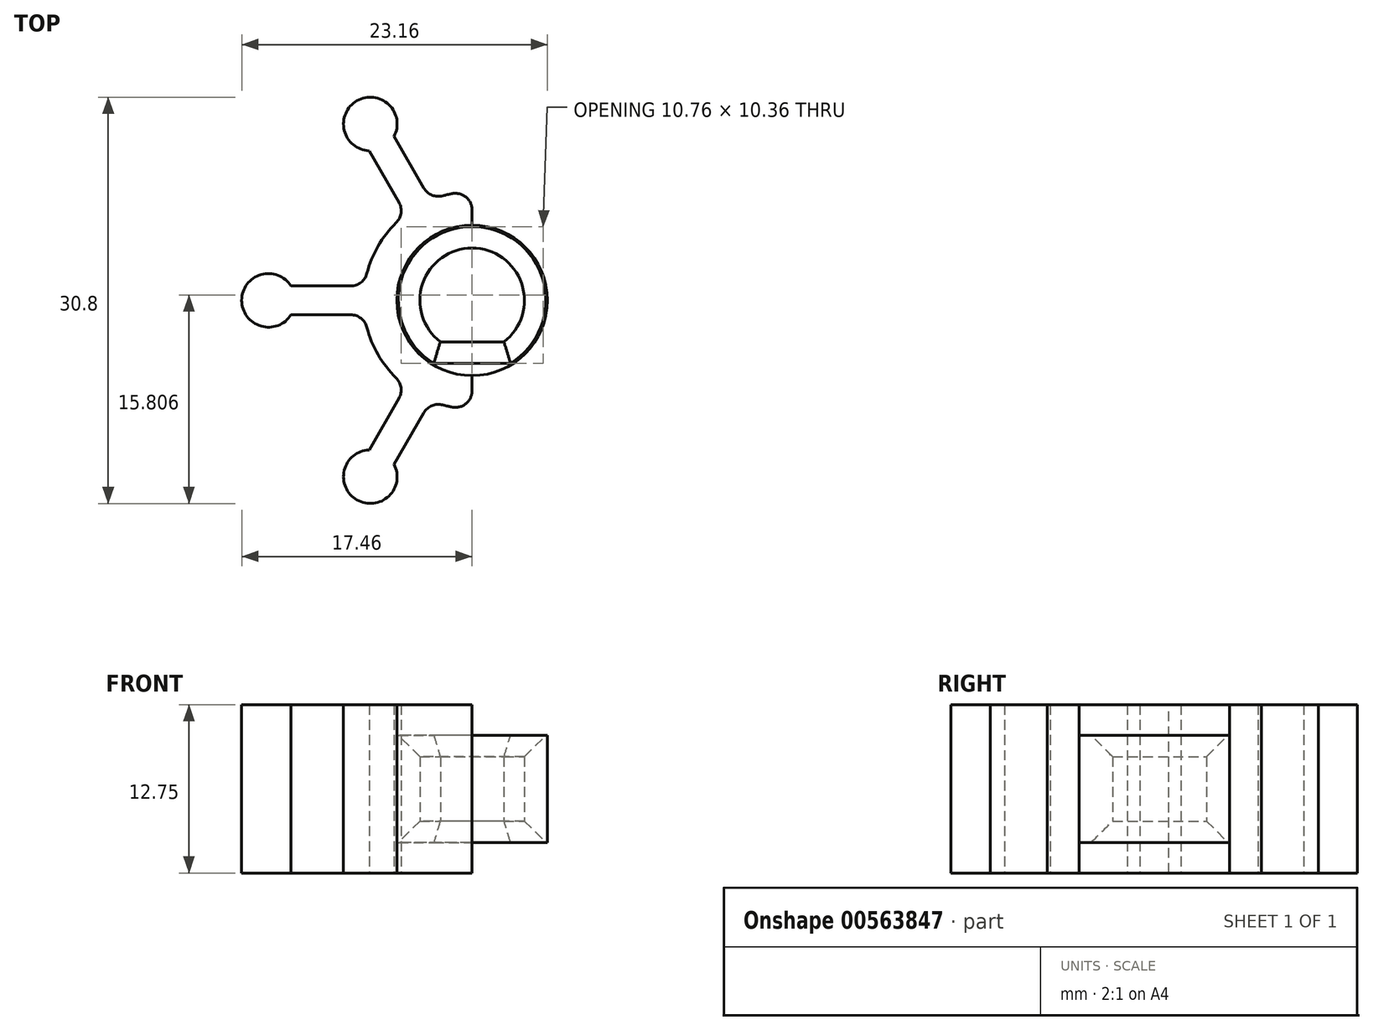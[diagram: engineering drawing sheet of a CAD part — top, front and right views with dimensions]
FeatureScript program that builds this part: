
annotation { "Feature Type Name" : "Feature", "Feature Type Description" : "" }
export const myFeature = defineFeature(function(context is Context, id is Id, definition is map)
    precondition{}
    {
        {
            var Q0;
            Q0=qCreatedBy(makeId("Top.planeOp"),FACE);
            var sketch = newSketch(context, id + "F0", { "sketchPlane" : qUnion([Q0])});
            skCircle(sketch, "E0", {"center": v(0, 0) * mm, "radius": 5.7 * mm});
            skArc(sketch, "E1", {"start": v(-3.13, -7.61) * mm, "mid": v(0, -8.23) * mm, "end": v(3.13, -7.61) * mm});
            skArc(sketch, "E2", {"start": v(2.4, -3.15) * mm, "mid": v(0, 3.96) * mm, "end": v(-2.4, -3.15) * mm});
            skLineSegment(sketch, "E3.trimOffspring", {"start": v(2.4, -3.15) * mm, "end": v(-2.4, -3.15) * mm});
            skLineSegment(sketch, "E4", {"start": v(8.23, 0) * mm, "end": v(19.44, 0) * mm});
            skLineSegment(sketch, "E5.3.0", {"start": v(-8.16, -1.1) * mm, "end": v(-13.72, -1.1) * mm});
            skLineSegment(sketch, "E5.3.1", {"start": v(-8.16, 1.1) * mm, "end": v(-13.72, 1.1) * mm});
            skPoint(sketch, "E6.orphan", {"position": v(-8.23, 1.1) * mm});
            skPoint(sketch, "E7.orphan", {"position": v(-8.23, -1.1) * mm});
            skPoint(sketch, "E8.orphan", {"position": v(-5.06, -6.58) * mm});
            skPoint(sketch, "E9.orphan", {"position": v(-3.17, -7.67) * mm});
            skPoint(sketch, "E10.orphan", {"position": v(3.17, -7.67) * mm});
            skPoint(sketch, "E11.orphan", {"position": v(5.06, -6.58) * mm});
            skPoint(sketch, "E12.orphan", {"position": v(8.23, -1.1) * mm});
            skPoint(sketch, "E13.orphan", {"position": v(8.23, 1.1) * mm});
            skPoint(sketch, "E14.orphan", {"position": v(5.06, 6.58) * mm});
            skPoint(sketch, "E15.orphan", {"position": v(3.17, 7.67) * mm});
            skPoint(sketch, "E16.orphan", {"position": v(-3.17, 7.67) * mm});
            skPoint(sketch, "E17.orphan", {"position": v(-5.06, 6.58) * mm});
            skArc(sketch, "E18.trimOffspring", {"start": v(5.02, -6.52) * mm, "mid": v(7.13, -4.11) * mm, "end": v(8.16, -1.1) * mm});
            skArc(sketch, "E19.trimOffspring", {"start": v(8.16, 1.1) * mm, "mid": v(7.13, 4.11) * mm, "end": v(5.02, 6.52) * mm});
            skArc(sketch, "E20.trimOffspring", {"start": v(3.13, 7.61) * mm, "mid": v(0, 8.23) * mm, "end": v(-3.13, 7.61) * mm});
            skArc(sketch, "E21.trimOffspring", {"start": v(-5.02, 6.52) * mm, "mid": v(-7.13, 4.11) * mm, "end": v(-8.16, 1.1) * mm});
            skArc(sketch, "E22.trimOffspring", {"start": v(-8.16, -1.1) * mm, "mid": v(-7.13, -4.11) * mm, "end": v(-5.02, -6.52) * mm});
            skLineSegment(sketch, "E23", {"start": v(0, 22.03) * mm, "end": v(0, -32.43) * mm});
            skArc(sketch, "E24", {"start": v(-13.72, 1.1) * mm, "mid": v(-17.46, 0) * mm, "end": v(-13.72, -1.1) * mm});
            skArc(sketch, "E25.1.0", {"start": v(-7.8, -11.33) * mm, "mid": v(-8.73, -15.12) * mm, "end": v(-5.91, -12.43) * mm});
            skLineSegment(sketch, "E25.1.1", {"start": v(-3.13, -7.61) * mm, "end": v(-5.91, -12.43) * mm});
            skLineSegment(sketch, "E25.1.2", {"start": v(-5.02, -6.52) * mm, "end": v(-7.8, -11.33) * mm});
            skArc(sketch, "E25.2.0", {"start": v(5.91, -12.43) * mm, "mid": v(8.73, -15.12) * mm, "end": v(7.8, -11.33) * mm});
            skLineSegment(sketch, "E25.2.1", {"start": v(5.02, -6.52) * mm, "end": v(7.8, -11.33) * mm});
            skLineSegment(sketch, "E25.2.2", {"start": v(3.13, -7.61) * mm, "end": v(5.91, -12.43) * mm});
            skArc(sketch, "E25.3.0", {"start": v(13.72, -1.1) * mm, "mid": v(17.46, 0) * mm, "end": v(13.72, 1.1) * mm});
            skLineSegment(sketch, "E25.3.1", {"start": v(8.16, 1.1) * mm, "end": v(13.72, 1.1) * mm});
            skLineSegment(sketch, "E25.3.2", {"start": v(8.16, -1.1) * mm, "end": v(13.72, -1.1) * mm});
            skArc(sketch, "E25.4.0", {"start": v(7.8, 11.33) * mm, "mid": v(8.73, 15.12) * mm, "end": v(5.91, 12.43) * mm});
            skLineSegment(sketch, "E25.4.1", {"start": v(3.13, 7.61) * mm, "end": v(5.91, 12.43) * mm});
            skLineSegment(sketch, "E25.4.2", {"start": v(5.02, 6.52) * mm, "end": v(7.8, 11.33) * mm});
            skArc(sketch, "E25.5.0", {"start": v(-5.91, 12.43) * mm, "mid": v(-8.73, 15.12) * mm, "end": v(-7.8, 11.33) * mm});
            skLineSegment(sketch, "E25.5.1", {"start": v(-5.02, 6.52) * mm, "end": v(-7.8, 11.33) * mm});
            skLineSegment(sketch, "E25.5.2", {"start": v(-3.13, 7.61) * mm, "end": v(-5.91, 12.43) * mm});
            skSolve(sketch);
        }
        {
            var Q0;
            {var subQ0=sQuery(id+"F0.wireOp",EDGE,"E5.2.2");var subQ1=makeQuery(id+"F0.imprint","IMPRINT",VERTEX,{"disambiguationData":[OD(0.0)],"derivedFrom":subQ0});Q0=makeQuery(id+"F0.imprint","IMPRINT",FACE,{"disambiguationData":[TD([[makeQuery(id+"F0.imprint","IMPRINT",EDGE,{"disambiguationData":[TD([[subQ1,-1.0]])],"derivedFrom":subQ0}),1.0]])]});}
            var Q1;
            {var subQ0=sQuery(id+"F0.wireOp",EDGE,"E5.1.2");var subQ1=makeQuery(id+"F0.imprint","IMPRINT",VERTEX,{"disambiguationData":[OD(0.0)],"derivedFrom":subQ0});Q1=makeQuery(id+"F0.imprint","IMPRINT",FACE,{"disambiguationData":[TD([[makeQuery(id+"F0.imprint","IMPRINT",EDGE,{"disambiguationData":[TD([[subQ1,-1.0]])],"derivedFrom":subQ0}),1.0]])]});}
            var Q2;
            {var subQ0=sQuery(id+"F0.wireOp",EDGE,"E5.3.2");var subQ1=makeQuery(id+"F0.imprint","IMPRINT",VERTEX,{"disambiguationData":[OD(0.0)],"derivedFrom":subQ0});Q2=makeQuery(id+"F0.imprint","IMPRINT",FACE,{"disambiguationData":[TD([[makeQuery(id+"F0.imprint","IMPRINT",EDGE,{"disambiguationData":[TD([[subQ1,-1.0]])],"derivedFrom":subQ0}),1.0]])]});}
            var Q3;
            {var subQ0=sQuery(id+"F0.wireOp",EDGE,"E5.4.2");var subQ1=makeQuery(id+"F0.imprint","IMPRINT",VERTEX,{"disambiguationData":[OD(0.0)],"derivedFrom":subQ0});Q3=makeQuery(id+"F0.imprint","IMPRINT",FACE,{"disambiguationData":[TD([[makeQuery(id+"F0.imprint","IMPRINT",EDGE,{"disambiguationData":[TD([[subQ1,-1.0]])],"derivedFrom":subQ0}),1.0]])]});}
            var Q4;
            {var subQ0=sQuery(id+"F0.wireOp",EDGE,"E5.5.2");var subQ1=makeQuery(id+"F0.imprint","IMPRINT",VERTEX,{"disambiguationData":[OD(0.0)],"derivedFrom":subQ0});Q4=makeQuery(id+"F0.imprint","IMPRINT",FACE,{"disambiguationData":[TD([[makeQuery(id+"F0.imprint","IMPRINT",EDGE,{"disambiguationData":[TD([[subQ1,-1.0]])],"derivedFrom":subQ0}),1.0]])]});}
            var Q5;
            {var subQ0=sQuery(id+"F0.wireOp",EDGE,"7pvLuRGC-pAmV-OfSB-9tyC-524oxxpyzLNE");var subQ1=makeQuery(id+"F0.imprint","IMPRINT",VERTEX,{"disambiguationData":[OD(0.0)],"derivedFrom":subQ0});Q5=makeQuery(id+"F0.imprint","IMPRINT",FACE,{"disambiguationData":[TD([[makeQuery(id+"F0.imprint","IMPRINT",EDGE,{"disambiguationData":[TD([[subQ1,1.0]])],"derivedFrom":subQ0}),1.0]])]});}
            var Q6;
            Q6=makeQuery(id+"F0.imprint","IMPRINT",FACE,{"disambiguationData":[TD([[makeQuery(id+"F0.imprint","IMPRINT",EDGE,{"derivedFrom":sQuery(id+"F0.wireOp",EDGE,"E0")}),-1.0]])]});
            extrude(context, id + "F1", {"entities" : qUnion([Q0, Q1, Q2, Q3, Q4, Q5, Q6]), "depth" : 12.75 * mm, "offsetDistance" : 25.4 * mm});
        }
        {
            var Q0;
            Q0=makeQuery(id+"F0.imprint","IMPRINT",FACE,{"disambiguationData":[TD([[makeQuery(id+"F0.imprint","IMPRINT",EDGE,{"derivedFrom":sQuery(id+"F0.wireOp",EDGE,"E0")}),1.0]])]});
            extrude(context, id + "F2", {"entities" : qUnion([Q0]), "operationType" : NewBodyOperationType.ADD, "depth" : 10.44 * mm, "offsetDistance" : 25.4 * mm, "hasSecondDirection" : true, "secondDirectionOppositeDirection" : true, "secondDirectionDepth" : -2.31 * mm});
        }
        {
            var Q0;
            Q0=makeQuery(id+"F1.opExtrude","SWEPT_EDGE",EDGE,{"disambiguationData":[OSD([sQuery(id+"F0.wireOp",EDGE,"E5.2.0"),sQuery(id+"F0.wireOp",EDGE,"E21.trimOffspring")])]});
            var Q1;
            Q1=makeQuery(id+"F1.opExtrude","SWEPT_EDGE",EDGE,{"disambiguationData":[OSD([sQuery(id+"F0.wireOp",EDGE,"E5.3.1"),sQuery(id+"F0.wireOp",EDGE,"E21.trimOffspring")])]});
            var Q2;
            Q2=makeQuery(id+"F1.opExtrude","SWEPT_EDGE",EDGE,{"disambiguationData":[OSD([sQuery(id+"F0.wireOp",EDGE,"E5.1.0"),sQuery(id+"F0.wireOp",EDGE,"E20.trimOffspring")])]});
            var Q3;
            Q3=makeQuery(id+"F1.opExtrude","SWEPT_EDGE",EDGE,{"disambiguationData":[OSD([sQuery(id+"F0.wireOp",EDGE,"E5.2.1"),sQuery(id+"F0.wireOp",EDGE,"E20.trimOffspring")])]});
            var Q4;
            Q4=makeQuery(id+"F1.opExtrude","SWEPT_EDGE",EDGE,{"disambiguationData":[OSD([sQuery(id+"F0.wireOp",EDGE,"65c7d86f-200b-4b3f-931e-3c375e95b6e6.0"),sQuery(id+"F0.wireOp",EDGE,"E19.trimOffspring")])]});
            var Q5;
            Q5=makeQuery(id+"F1.opExtrude","SWEPT_EDGE",EDGE,{"disambiguationData":[OSD([sQuery(id+"F0.wireOp",EDGE,"E5.1.1"),sQuery(id+"F0.wireOp",EDGE,"E19.trimOffspring")])]});
            var Q6;
            Q6=makeQuery(id+"F1.opExtrude","SWEPT_EDGE",EDGE,{"disambiguationData":[OSD([sQuery(id+"F0.wireOp",EDGE,"7135fc8a-2f7a-4ffa-b230-452bec902163.0"),sQuery(id+"F0.wireOp",EDGE,"E18.trimOffspring")])]});
            var Q7;
            Q7=makeQuery(id+"F1.opExtrude","SWEPT_EDGE",EDGE,{"disambiguationData":[OSD([sQuery(id+"F0.wireOp",EDGE,"E5.5.0"),sQuery(id+"F0.wireOp",EDGE,"E18.trimOffspring")])]});
            var Q8;
            Q8=makeQuery(id+"F1.opExtrude","SWEPT_EDGE",EDGE,{"disambiguationData":[OSD([sQuery(id+"F0.wireOp",EDGE,"E1"),sQuery(id+"F0.wireOp",EDGE,"E5.5.1")])]});
            var Q9;
            Q9=makeQuery(id+"F1.opExtrude","SWEPT_EDGE",EDGE,{"disambiguationData":[OSD([sQuery(id+"F0.wireOp",EDGE,"E1"),sQuery(id+"F0.wireOp",EDGE,"E5.4.0")])]});
            var Q10;
            Q10=makeQuery(id+"F1.opExtrude","SWEPT_EDGE",EDGE,{"disambiguationData":[OSD([sQuery(id+"F0.wireOp",EDGE,"E5.4.1"),sQuery(id+"F0.wireOp",EDGE,"E22.trimOffspring")])]});
            var Q11;
            Q11=makeQuery(id+"F1.opExtrude","SWEPT_EDGE",EDGE,{"disambiguationData":[OSD([sQuery(id+"F0.wireOp",EDGE,"E5.3.0"),sQuery(id+"F0.wireOp",EDGE,"E22.trimOffspring")])]});
            fillet(context, id + "F3", {"entities" : qUnion([Q0, Q1, Q2, Q3, Q4, Q5, Q6, Q7, Q8, Q9, Q10, Q11]), "radius" : 1.27 * mm, "tangentPropagation" : true, "allowEdgeOverflow" : false});
        }
        {
            var Q0;
            Q0=makeQuery(id+"F2.opExtrude","CAP_EDGE",EDGE,{"disambiguationData":[OSD([sQuery(id+"F0.wireOp",EDGE,"E2")])],"isStart":false});
            var Q1;
            Q1=makeQuery(id+"F2.opExtrude","CAP_EDGE",EDGE,{"disambiguationData":[OSD([sQuery(id+"F0.wireOp",EDGE,"E3.trimOffspring")])],"isStart":false});
            var Q2;
            Q2=makeQuery(id+"F2.opExtrude","CAP_EDGE",EDGE,{"disambiguationData":[OSD([sQuery(id+"F0.wireOp",EDGE,"E2")])],"isStart":true});
            var Q3;
            Q3=makeQuery(id+"F2.opExtrude","CAP_EDGE",EDGE,{"disambiguationData":[OSD([sQuery(id+"F0.wireOp",EDGE,"E3.trimOffspring")])],"isStart":true});
            chamfer(context, id + "F4", {"entities" : qUnion([Q0, Q1, Q2, Q3]), "width" : 1.63 * mm, "tangentPropagation" : true});
        }
    });
